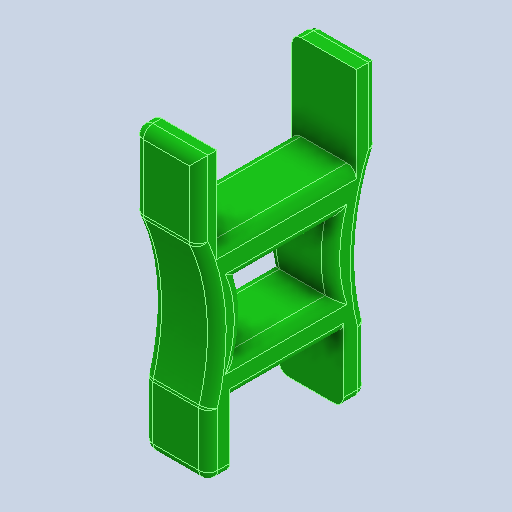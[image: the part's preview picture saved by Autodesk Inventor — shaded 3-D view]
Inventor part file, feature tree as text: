
AUTODESK INVENTOR PART (.ipt)
format: ipt  version: 2022 (Build 260153000, 153)  size: 226,816 bytes
history: native  units: in
note: dims shown in document units (in); Inventor stores cm internally (conversion verified against a paired STEP export)
features: extrude x1, fillet x1, sketch x1
ambient origin geometry x8: Origin, YZ Plane, XZ Plane, XY Plane, X Axis, Y Axis, Z Axis, Center Point
bodies: Body1 (feature_tree)
feature tree (3):
  extrude  "Extrusion2"  Depth=0.125in
  fillet  "Fillet2"  [1 undecoded]
  sketch  "Sketch2"  dims[d3=0.8661in d4=0.0in d5=0.125in]
note: 1 required parameter value undecoded (feature->parameter linkage not recoverable at this tier; creation-order binding heuristic only, values carry confidence <= 0.55)
